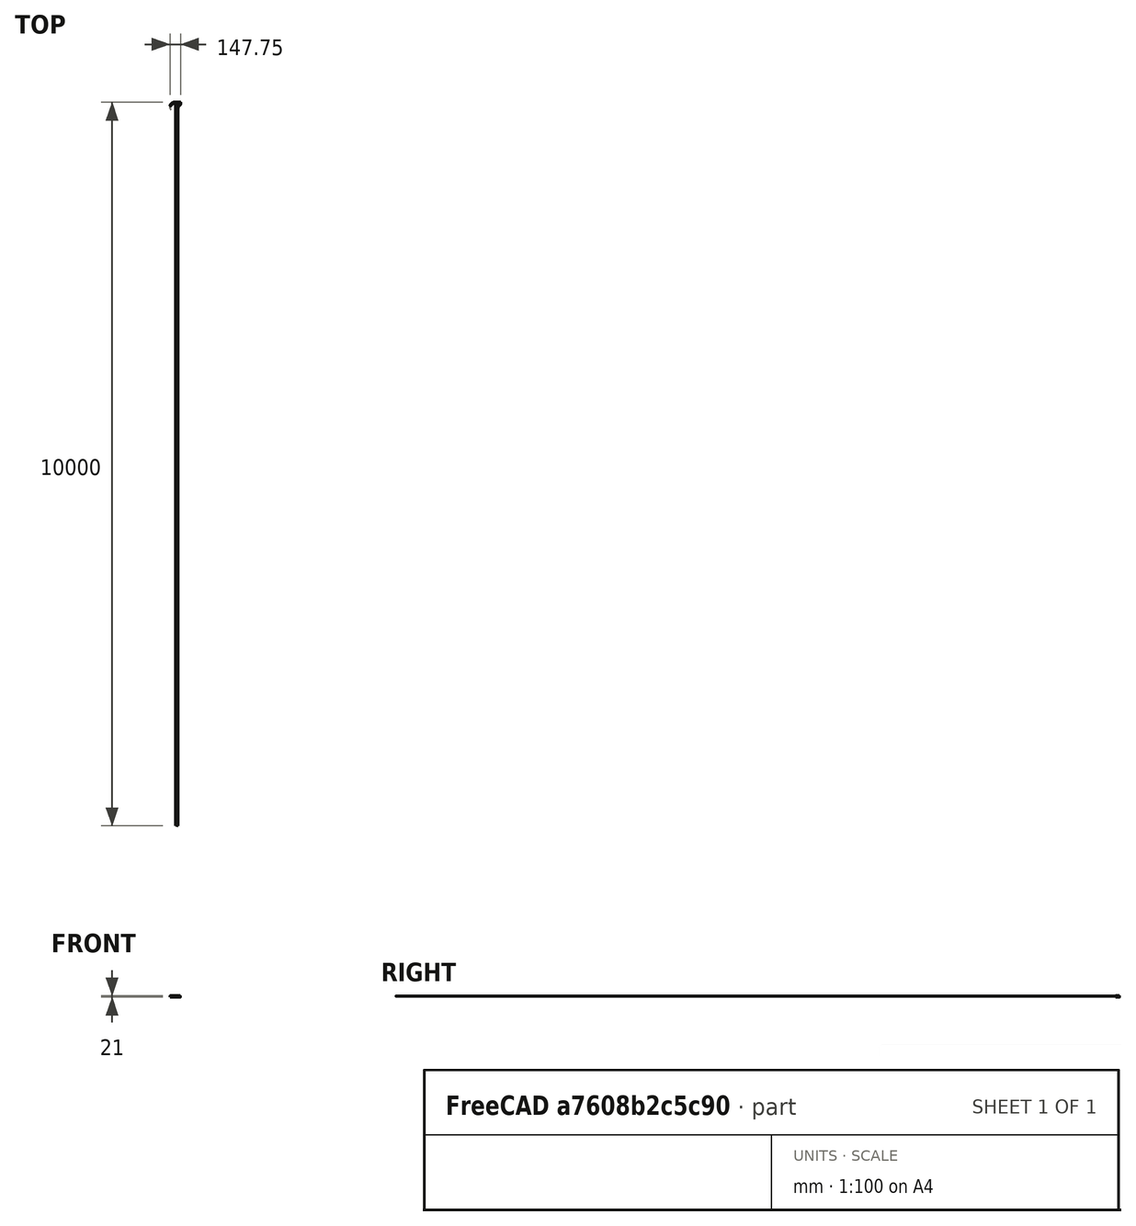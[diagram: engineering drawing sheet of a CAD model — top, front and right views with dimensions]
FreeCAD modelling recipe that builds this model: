
FCSTD DOCUMENT  (FreeCAD 0.16R)
Label: V3
License: All rights reserved
LicenseURL: http://en.wikipedia.org/wiki/All_rights_reserved
objects: Sketcher::SketchObject×4, PartDesign::Pad×3, PartDesign::Fillet×2, PartDesign::Pocket×1, Mesh::Feature×1
note: 14 computed .brp shape members not serialized (recipe doc carries the construction recipe); baked Part::Feature solids carry a one-line shape summary decoded from their .brp

FEATURE [Sketcher::SketchObject] Sketch
  sketch-geometry (11):
    g0: ArcOfCircle CenterX=0 CenterY=0 CenterZ=0 NormalX=0 NormalY=0 NormalZ=1 Radius=65 StartAngle=1.5708 EndAngle=2.86744
    g1: ArcOfCircle CenterX=0 CenterY=0 CenterZ=0 NormalX=0 NormalY=0 NormalZ=1 Radius=48 StartAngle=0.377003 EndAngle=2.75854
    g2: LineSegment StartX=2.40667e-07 StartY=65 StartZ=0 EndX=79.4942 EndY=65 EndZ=0
    g3: LineSegment StartX=47.168 StartY=15.3736 StartZ=0 EndX=54.9232 EndY=15.3842 EndZ=0
    g4: LineSegment StartX=84.8824 StartY=59.6118 StartZ=0 EndX=84.8824 EndY=45.3841 EndZ=0
    g5: ArcOfCircle CenterX=54.8824 CenterY=45.3841 CenterZ=0 NormalX=0 NormalY=0 NormalZ=1 Radius=30 StartAngle=4.71375 EndAngle=6.28319
    g6: ArcOfCircle CenterX=79.4942 CenterY=59.6118 CenterZ=0 NormalX=0 NormalY=0 NormalZ=1 Radius=5.38817 StartAngle=0 EndAngle=1.5708
    g7: ArcOfCircle CenterX=49.0502 CenterY=20.0058 CenterZ=0 NormalX=0 NormalY=0 NormalZ=1 Radius=5 StartAngle=3.62755 EndAngle=4.32643
    g8: ArcOfCircle CenterX=-60.5912 CenterY=17.3257 CenterZ=0 NormalX=0 NormalY=0 NormalZ=1 Radius=2 StartAngle=3.00536 EndAngle=4.40537
    g9: ArcOfCircle CenterX=-48.9002 CenterY=20.3538 CenterZ=0 NormalX=0 NormalY=0 NormalZ=1 Radius=5 StartAngle=4.8743 EndAngle=5.77943
    g10: LineSegment StartX=-61.1956 StartY=15.4192 StartZ=0 EndX=-48.0942 EndY=15.4192 EndZ=0
  constraints (35):
    c: Radius(g0) = 65
    c: Coincident(g-1,g0)
    c: PointOnObject(g1,g-2)
    c: Coincident(g1,g-1)
    c: Radius(g1) = 48
    c: Horizontal(g2)
    c: Coincident(g0,g2)
    c: Vertical(g4)
    c: Tangent(g4,g5) = 1.5708
    c: Tangent(g3,g5) = -1.5708
    c: Tangent(g4,g6) = 1.5708
    c: Tangent(g2,g6) = 1.5708
    c: Radius(g7) = 5
    c: Radius(g9) = 5
    c: Radius(g8) = 2
    c: Coincident(g3,g7)
    c: Coincident(g1,g7)
    c: Coincident(g10,g9)
    c: Coincident(g1,g9)
    c: Coincident(g10,g8)
    c: Coincident(g0,g8)
    c: Distance(g10) = 13.1014
    c: Distance(g2) = 79.4942
    c: Distance(g3) = 7.75526
    c: Distance(g4) = 14.2277
    c: Radius(g5) = 30
    c: Radius(g6) = 5.38817
    c: DistanceY(g-1,g2) = 65
    c: DistanceY(g3) = 15.3736
    c: DistanceY(g9) = 15.4192
    c: DistanceY(g0) = 17.5973
    c: DistanceY(g1) = 17.9402
    c: DistanceY(g8) = 15.4192
    c: DistanceY(g1) = 17.6705
    c: DistanceX(g8) = -61.1956
FEATURE [Sketcher::SketchObject] Sketch002
  Placement = pos=(0,0,1) rot=(0,0,1;0rad)
  sketch-geometry (8):
    g0: ArcOfCircle CenterX=0 CenterY=0 CenterZ=0 NormalX=0 NormalY=0 NormalZ=1 Radius=48 StartAngle=0.377003 EndAngle=2.75854
    g1: LineSegment StartX=47.0328 StartY=15.3736 StartZ=0 EndX=54.7867 EndY=15.2303 EndZ=0
    g2: ArcOfCircle CenterX=55.341 CenterY=45.2252 CenterZ=0 NormalX=0 NormalY=0 NormalZ=1 Radius=30 StartAngle=4.69391 EndAngle=6.10812
    g3: ArcOfCircle CenterX=49.0887 CenterY=19.9313 CenterZ=0 NormalX=0 NormalY=0 NormalZ=1 Radius=5 StartAngle=3.61079 EndAngle=4.28863
    g4: ArcOfCircle CenterX=-48.9021 CenterY=20.3504 CenterZ=0 NormalX=0 NormalY=0 NormalZ=1 Radius=5 StartAngle=4.91142 EndAngle=5.7802
    g5: ArcOfCircle CenterX=-0.655187 CenterY=1.27485 CenterZ=0 NormalX=0 NormalY=0 NormalZ=1 Radius=51 StartAngle=0.862262 EndAngle=2.75615
    g6: LineSegment StartX=84.8825 StartY=40 StartZ=0 EndX=32.5316 EndY=40 EndZ=0
    g7: LineSegment StartX=-47.9135 StartY=20.4491 StartZ=0 EndX=-47.9135 EndY=15.4491 EndZ=0
  constraints (29):
    c: PointOnObject(g0,g-2)
    c: Coincident(g0,g-1)
    c: Radius(g0) = 48
    c: Tangent(g1,g2) = -1.5708
    c: Radius(g3) = 5
    c: Radius(g4) = 5
    c: Coincident(g1,g3)
    c: Coincident(g0,g3)
    c: Coincident(g0,g4)
    c: Distance(g1) = 7.75526
    c: Radius(g2) = 30
    c: DistanceY(g1) = 15.3736
    c: DistanceY(g0) = 17.9402
    c: DistanceY(g0) = 17.6705
    c: DistanceX(g4,g5) = 0
    c: DistanceX(g5) = -47.9135
    c: DistanceY(g4) = 15.4491
    c: DistanceY(g4,g5) = 5
    c: Radius(g5) = 51
    c: Coincident(g6,g2)
    c: Coincident(g5,g6)
    c: Vertical(g7)
    c: Coincident(g7,g5)
    c: Coincident(g7,g4)
    c: DistanceY(g5) = 40
    c: DistanceX(g2) = 84.8825
    c: DistanceY(g1) = 15.2303
    c: DistanceX(g5) = 32.5316
    c: Horizontal(g6)
FEATURE [PartDesign::Pad] Pad002  label="Stiffener"
  Length = 1
  Length2 = 100
  Placement = pos=(0,0,1) rot=(0,0,1;0rad)
  Sketch = -> Sketch002
  Type = 0
FEATURE [PartDesign::Pad] Pad  label="Faceplate"
  Length = 1
  Length2 = 100
  Sketch = -> Sketch
  Type = 0
FEATURE [Sketcher::SketchObject] Sketch001
  Placement = pos=(0,0,1) rot=(0,0,1;0rad)
  Support = -> Pad [Face13]
  sketch-geometry (6):
    g0: ArcOfCircle CenterX=0 CenterY=0 CenterZ=0 NormalX=0 NormalY=0 NormalZ=1 Radius=65 StartAngle=1.5708 EndAngle=2.88461
    g1: LineSegment StartX=6.04881e-05 StartY=65 StartZ=0 EndX=80.0001 EndY=65 EndZ=0
    g2: LineSegment StartX=80.0001 StartY=63 StartZ=0 EndX=6.04881e-05 EndY=63 EndZ=0
    g3: LineSegment StartX=80.0001 StartY=65 StartZ=0 EndX=80.0001 EndY=63 EndZ=0
    g4: ArcOfCircle CenterX=0.26057 CenterY=1.00055 CenterZ=0 NormalX=0 NormalY=0 NormalZ=1 Radius=62 StartAngle=1.575 EndAngle=2.88858
    g5: LineSegment StartX=-62.8655 StartY=16.5204 StartZ=0 EndX=-59.7655 EndY=16.5204 EndZ=0
  constraints (19):
    c: Radius(g0) = 65
    c: Coincident(g-1,g0)
    c: Horizontal(g1)
    c: Coincident(g0,g1)
    c: DistanceY(g-1,g1) = 65
    c: Horizontal(g2)
    c: Equal(g2,g1)
    c: DistanceX(g0,g2) = 0
    c: Coincident(g3,g2)
    c: Coincident(g3,g1)
    c: DistanceY(g2,g1) = 2
    c: Radius(g4) = 62
    c: Coincident(g4,g2)
    c: DistanceX(g0,g4) = 3.1
    c: DistanceY(g4,g0) = 0
    c: DistanceY(g-1,g0) = 16.5204
    c: Coincident(g4,g5)
    c: Coincident(g5,g0)
    c: Distance(g1) = 80
FEATURE [PartDesign::Pad] Pad004  label="Connector"
  Length = 20
  Length2 = 100
  Sketch = -> Sketch001
  Type = 0
FEATURE [PartDesign::Fillet] Fillet
  Base = -> Pad004 [Edge52]
  Radius = 10
FEATURE [PartDesign::Fillet] Fillet001
  Base = -> Fillet [Edge25]
  Radius = 2
FEATURE [Sketcher::SketchObject] Sketch003
  ExternalGeometry = -> [Fillet001]
  Placement = pos=(0,65,0) rot=(0,0.707107,0.707107;3.14159rad)
  Support = -> Fillet001 [Face4]
  sketch-geometry (3):
    g0: Circle CenterX=-42.4001 CenterY=15.5 CenterZ=0 NormalX=0 NormalY=0 NormalZ=1 Radius=2
    g1: Circle CenterX=-28.5001 CenterY=15.5 CenterZ=0 NormalX=0 NormalY=0 NormalZ=1 Radius=2
    g2: Circle CenterX=-14.5001 CenterY=15.5 CenterZ=0 NormalX=0 NormalY=0 NormalZ=1 Radius=2
  constraints (9):
    c: Radius(g2) = 2
    c: Equal(g2,g1)
    c: Equal(g2,g0)
    c: DistanceX(g-5,g0) = 37.6
    c: DistanceX(g-5,g1) = 51.5
    c: DistanceX(g-5,g2) = 65.5
    c: Distance(g0,g-4) = 5.5
    c: Distance(g1,g-4) = 5.5
    c: Distance(g2,g-4) = 5.5
FEATURE [PartDesign::Pocket] Pocket
  Length = 5
  Sketch = -> Sketch003
  Type = 1
FEATURE [Mesh::Feature] Mesh  label="Pocket (Meshed)"
